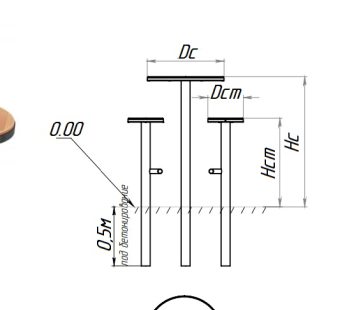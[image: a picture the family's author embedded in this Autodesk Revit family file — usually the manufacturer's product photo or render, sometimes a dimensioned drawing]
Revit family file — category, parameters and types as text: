
# Revit family: Комплект барной мебели «Таверна» Арт 19652
name_source: partatom
category: Антураж
revit_build: Autodesk Revit 2018 (Build: 20180423_1000(x64)
units: mm (PartAtom-declared; Revit-internal decimal feet)

## family parameters
Всегда вертикально = Да
Источник визуального образа = Геометрия семейства
На основе рабочей плоскости = Нет
Общий = Нет
При загрузке вырезать с полостями = Нет
Точка расчета площади = Нет

## types (2) — shared parameters
URL = https://hobbyka.ru
Артикул товара = Арт. 19652
Группа модели = Комплекты садовой мебели
Изготовитель = ООО «Хоббика»
Изображение типоразмера = Комплект барной мебели «Таверна» Арт 19652.jpg
Материал изделия = Сталь, дерево
Цвет каркаса = Сталь
Цвет отделки = Дерево

## per-type parameters (varying)
| type | Высота | Длина | Стол | Стул | Ширина |
| Комплект барной мебели «Таверна». Стол | 1100 мм | 650 мм | Да | Нет | 650 мм |
| Комплект барной мебели «Таверна». Стул | 750 мм | 300 мм | Нет | Да | 300 мм |

note: column(s) folded — value = type name in every type: Описание
